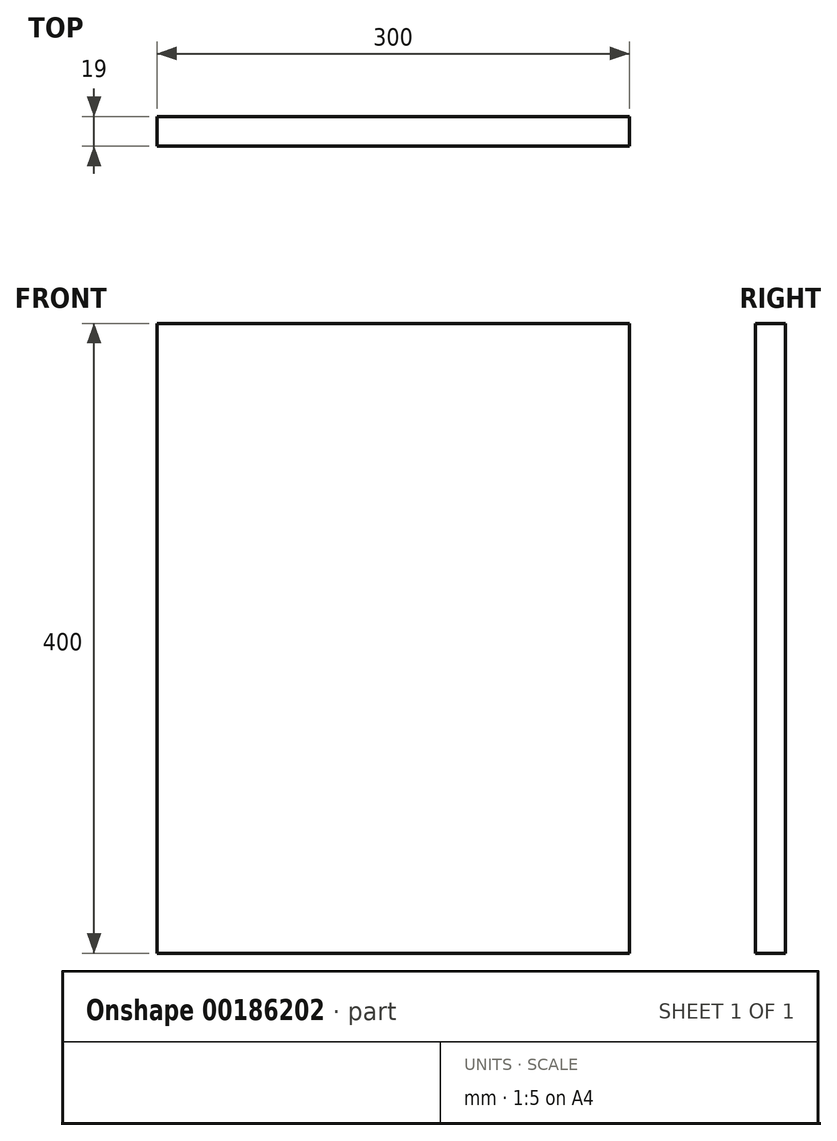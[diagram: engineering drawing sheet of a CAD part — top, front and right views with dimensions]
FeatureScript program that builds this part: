
annotation { "Feature Type Name" : "Feature", "Feature Type Description" : "" }
export const myFeature = defineFeature(function(context is Context, id is Id, definition is map)
    precondition{}
    {
        {
            var Q0;
            Q0=qCreatedBy(makeId("Front.planeOp"),FACE);
            var sketch = newSketch(context, id + "F0", { "sketchPlane" : qUnion([Q0])});
            skLineSegment(sketch, "E0.bottom", {"start": v(-154.82, 190.59) * mm, "end": v(145.18, 190.59) * mm});
            skLineSegment(sketch, "E0.top", {"start": v(-154.82, -209.41) * mm, "end": v(145.18, -209.41) * mm});
            skLineSegment(sketch, "E0.left", {"start": v(-154.82, 190.59) * mm, "end": v(-154.82, -209.41) * mm});
            skLineSegment(sketch, "E0.right", {"start": v(145.18, 190.59) * mm, "end": v(145.18, -209.41) * mm});
            skSolve(sketch);
        }
        {
            var Q0;
            Q0 = qSketchRegion(id + "F0", true);
            extrude(context, id + "F1", {"entities" : qUnion([Q0]), "depth" : 19 * mm});
        }
    });
